# Revit family: Specification-Grade-Style-Line-Receptacles
name_source: partatom
category: Electrical Fixtures
revit_build: Autodesk Revit MEP 2012 (Build: 20110916_2132(x64)
units: mm (PartAtom-declared; Revit-internal decimal feet)

## types (2) — shared parameters
Assembly Code = D5020100
Construction Details = http://www.hubbell-premise.com
Default Elevation = 1' - 6"
Description = Exectrical Fixture as specified in 26 05 00
Green Building-LEED = http://www.arcat.com
Installation-Fabrication = http://www.hubbell-premise.com
Keynote = 26 05 00
Load Classification = Power
Manufacturer = Hubbell Wiring Devices - Kellems
Manufacturer Fax = 475-882-4849
Manufacturer Website = http://www.hubbell-wiring.com
Model = As specified in 26 05 00
Number of Poles = 1
Product Data = http://www.arcat.com
Sales Information = http://www.hubbell-wiring.com
Send Message = http://admin.arcat.com
Specification = http://www.arcat.com
Test Data = http://www.hubbell-premise.com
URL = http://www.hubbell-wiring.com
Voltage = 0
zero-valued in all types: DevType, Expected Lifespan (Years), Maintenance Schedule (Months), Warranty Duration (Years)

## type names (no varying parameters)
- Standard Receptacle
- Standard GFCI

note: source unit labels omitted for Voltage — the stored unit's dimension contradicts the parameter name (converter mislabeling)

## geometry (parser evidence)
native form markers: Blend x2, Sweep x6
no freeform markers — native parametric forms only
